# Revit family: sh-101
name_source: partatom
category: Lighting Fixtures
revit_build: Autodesk Revit 2017 (Build: 20160225_1515(x64)
units: mm (PartAtom-declared; Revit-internal decimal feet)

## family parameters
Always vertical = Yes
Cut with Voids When Loaded = No
Host = Wall
Light Source = Yes
OmniClass Number = 23.80.70.00
OmniClass Title = Lighting
Part Type = Normal
Room Calculation Point = No
Round Connector Dimension = Use Diameter
Shared = No

## types (3) — shared parameters
Body Material = Aluminum
Color Filter = 16777215
Dimming Lamp Color Temperature Shift = <None>
Emit Shape Visible in Rendering = No
Emit from Circle Diameter = 1 cm
Flicker = Free Flicker
Height = 15 cm
IP = IP54
Lamp = LED
Manufacturer = SHOA
Model = SH-101
Photometric Web File = BE_24218K3.IES
Protection Class = Class I
Tilt Angle = 90.00°
Type medule = SMD
URL = https://www.shoaco.com
Voltage/Frequency = 230V-50HZ
Website = www.shoaco.com
Width = 21 cm
color temperature = 3000K
consumption current = 0 A
instalation = wall mounted
wattage. = 12 W

## per-type parameters (varying)
| type | Body color |
| SH-101(Black Body-3000K-LED) | Black |
| SH-101(White Body-3000K-LED) | white |
| SH-101(Gray  Body-3000K-LED) | Gray body |

## geometry (parser evidence)
native form markers: Sweep x3
no freeform markers — native parametric forms only
